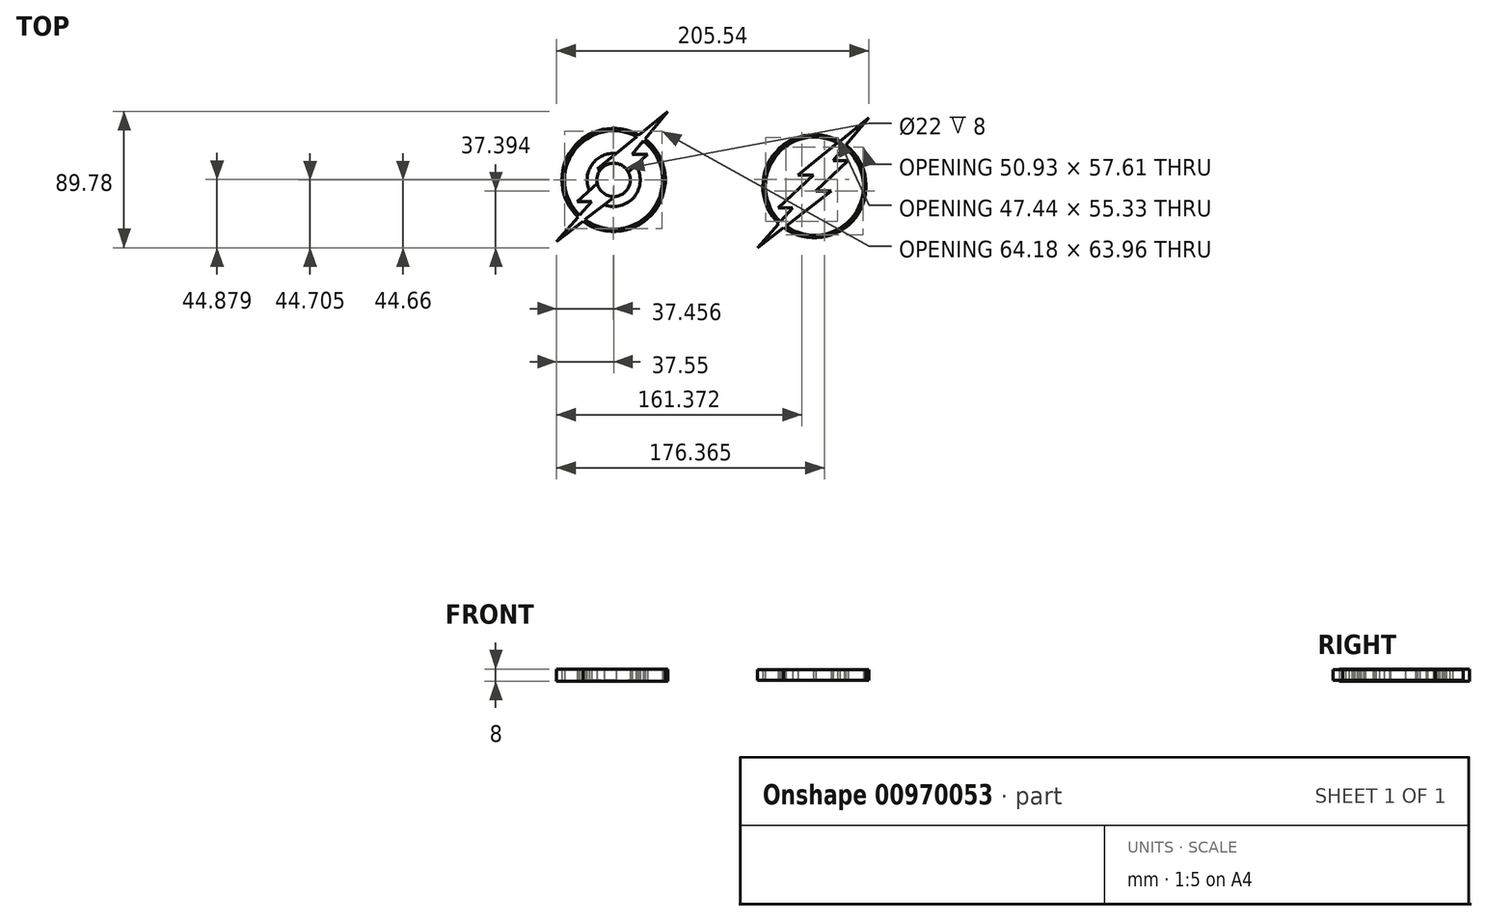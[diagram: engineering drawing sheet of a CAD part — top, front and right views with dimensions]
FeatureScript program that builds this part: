
annotation { "Feature Type Name" : "Feature", "Feature Type Description" : "" }
export const myFeature = defineFeature(function(context is Context, id is Id, definition is map)
    precondition{}
    {
        {
            var Q0;
            Q0=qCreatedBy(makeId("Top.planeOp"),FACE);
            var sketch = newSketch(context, id + "F0", { "sketchPlane" : qUnion([Q0])});
            skCircle(sketch, "E0", {"center": v(0, 0) * mm, "radius": 11 * mm});
            skPoint(sketch, "E1.first.point", {"position": v(112.01, 22.3) * mm});
            skPoint(sketch, "E1.second.point", {"position": v(163.3, -16.26) * mm});
            skPoint(sketch, "E1.third.point", {"position": v(117.87, -34.17) * mm});
            skLineSegment(sketch, "E2", {"start": v(94.73, -44.66) * mm, "end": v(108.79, -28.72) * mm});
            skLineSegment(sketch, "E3", {"start": v(117.9, -18.4) * mm, "end": v(108.37, -18.4) * mm});
            skLineSegment(sketch, "E4", {"start": v(108.37, -18.4) * mm, "end": v(131.53, 3.16) * mm});
            skLineSegment(sketch, "E5", {"start": v(131.53, 3.16) * mm, "end": v(121.52, 3.16) * mm});
            skLineSegment(sketch, "E6", {"start": v(121.52, 3.16) * mm, "end": v(147.54, 24.34) * mm});
            skLineSegment(sketch, "E7", {"start": v(167.99, 40.98) * mm, "end": v(152.98, 22.85) * mm});
            skLineSegment(sketch, "E8", {"start": v(144.46, 12.56) * mm, "end": v(154.5, 12.56) * mm});
            skLineSegment(sketch, "E9", {"start": v(154.5, 12.56) * mm, "end": v(133.25, -7.33) * mm});
            skLineSegment(sketch, "E10", {"start": v(133.25, -7.33) * mm, "end": v(143.2, -7.33) * mm});
            skLineSegment(sketch, "E11", {"start": v(143.2, -7.33) * mm, "end": v(113.35, -30.32) * mm});
            skArc(sketch, "E12.0", {"start": v(148.97, 25.5) * mm, "mid": v(104.96, 16.11) * mm, "end": v(108.79, -28.72) * mm});
            skArc(sketch, "E13.0", {"start": v(147.54, 24.34) * mm, "mid": v(106.15, 14.86) * mm, "end": v(109.91, -27.45) * mm});
            skLineSegment(sketch, "E14.trimOffspring", {"start": v(148.97, 25.5) * mm, "end": v(167.99, 40.98) * mm});
            skLineSegment(sketch, "E15.trimOffspring", {"start": v(151.9, 21.54) * mm, "end": v(144.46, 12.56) * mm});
            skArc(sketch, "E16.trimOffspring", {"start": v(113.35, -30.32) * mm, "mid": v(158.22, -23.41) * mm, "end": v(151.9, 21.54) * mm});
            skLineSegment(sketch, "E17.trimOffspring", {"start": v(109.91, -27.45) * mm, "end": v(117.9, -18.4) * mm});
            skArc(sketch, "E18.trimOffspring", {"start": v(111.95, -31.4) * mm, "mid": v(159.4, -24.65) * mm, "end": v(152.98, 22.85) * mm});
            skLineSegment(sketch, "E19.trimOffspring", {"start": v(111.95, -31.4) * mm, "end": v(94.73, -44.66) * mm});
            skLineSegment(sketch, "E20", {"start": v(2.42, 0) * mm, "end": v(132.28, -4.14) * mm, "construction": true});
            skCircle(sketch, "E21", {"center": v(0, 0) * mm, "radius": 17.5 * mm});
            skSolve(sketch);
        }
        {
            var Q0;
            Q0=makeQuery(id+"F0.imprint","IMPRINT",FACE,{"disambiguationData":[TD([[makeQuery(id+"F0.imprint","IMPRINT",EDGE,{"derivedFrom":sQuery(id+"F0.wireOp",EDGE,"E2")}),-1.0]])]});
            extrude(context, id + "F1", {"entities" : qUnion([Q0]), "endBound" : BoundingType.SYMMETRIC, "depth" : 8 * mm, "offsetDistance" : 25 * mm});
        }
        {
            var Q0;
            Q0=makeQuery(id+"F1.opExtrude","SWEPT_BODY",BODY,{"disambiguationData":[OSD([sQuery(id+"F0.wireOp",EDGE,"E2"),sQuery(id+"F0.wireOp",EDGE,"E3"),sQuery(id+"F0.wireOp",EDGE,"E4"),sQuery(id+"F0.wireOp",EDGE,"E5"),sQuery(id+"F0.wireOp",EDGE,"E6"),sQuery(id+"F0.wireOp",EDGE,"E7"),sQuery(id+"F0.wireOp",EDGE,"E8"),sQuery(id+"F0.wireOp",EDGE,"E9"),sQuery(id+"F0.wireOp",EDGE,"E10"),sQuery(id+"F0.wireOp",EDGE,"E11"),sQuery(id+"F0.wireOp",EDGE,"E12.0"),sQuery(id+"F0.wireOp",EDGE,"E13.0"),sQuery(id+"F0.wireOp",EDGE,"E14.trimOffspring"),sQuery(id+"F0.wireOp",EDGE,"E15.trimOffspring"),sQuery(id+"F0.wireOp",EDGE,"E16.trimOffspring"),sQuery(id+"F0.wireOp",EDGE,"E17.trimOffspring"),sQuery(id+"F0.wireOp",EDGE,"E18.trimOffspring"),sQuery(id+"F0.wireOp",EDGE,"E19.trimOffspring")])]});
            var Q1;
            Q1=sQuery(id+"F0.wireOp",VERTEX,"E20.end");
            var Q2;
            Q2=sQuery(id+"F0.wireOp",VERTEX,"E0.center");
            transform(context, id + "F2", {"entities" : qUnion([Q0]), "transformType" : TransformType.TRANSLATION_ENTITY, "oppositeDirectionEntity" : false, "transformLine" : qUnion([Q1, Q2]), "makeCopy" : false});
        }
        {
            var Q0;
            Q0=makeQuery(id+"F0.imprint","IMPRINT",FACE,{"disambiguationData":[TD([[makeQuery(id+"F0.imprint","IMPRINT",EDGE,{"derivedFrom":sQuery(id+"F0.wireOp",EDGE,"E2")}),-1.0]])]});
            var Q1;
            Q1=makeQuery(id+"F0.imprint","IMPRINT",FACE,{"disambiguationData":[TD([[makeQuery(id+"F0.imprint","IMPRINT",EDGE,{"derivedFrom":sQuery(id+"F0.wireOp",EDGE,"E0")}),-1.0]])]});
            extrude(context, id + "F3", {"entities" : qUnion([Q0, Q1]), "operationType" : NewBodyOperationType.ADD, "endBound" : BoundingType.SYMMETRIC, "depth" : 7 * mm, "offsetDistance" : 25 * mm});
        }
        {
            var Q0;
            Q0=makeQuery(id+"F0.imprint","IMPRINT",FACE,{"disambiguationData":[TD([[makeQuery(id+"F0.imprint","IMPRINT",EDGE,{"derivedFrom":sQuery(id+"F0.wireOp",EDGE,"E0")}),1.0]])]});
            extrude(context, id + "F4", {"entities" : qUnion([Q0]), "operationType" : NewBodyOperationType.REMOVE, "endBound" : BoundingType.SYMMETRIC, "oppositeDirection" : true, "depth" : 25 * mm, "offsetDistance" : 25 * mm});
        }
    });
